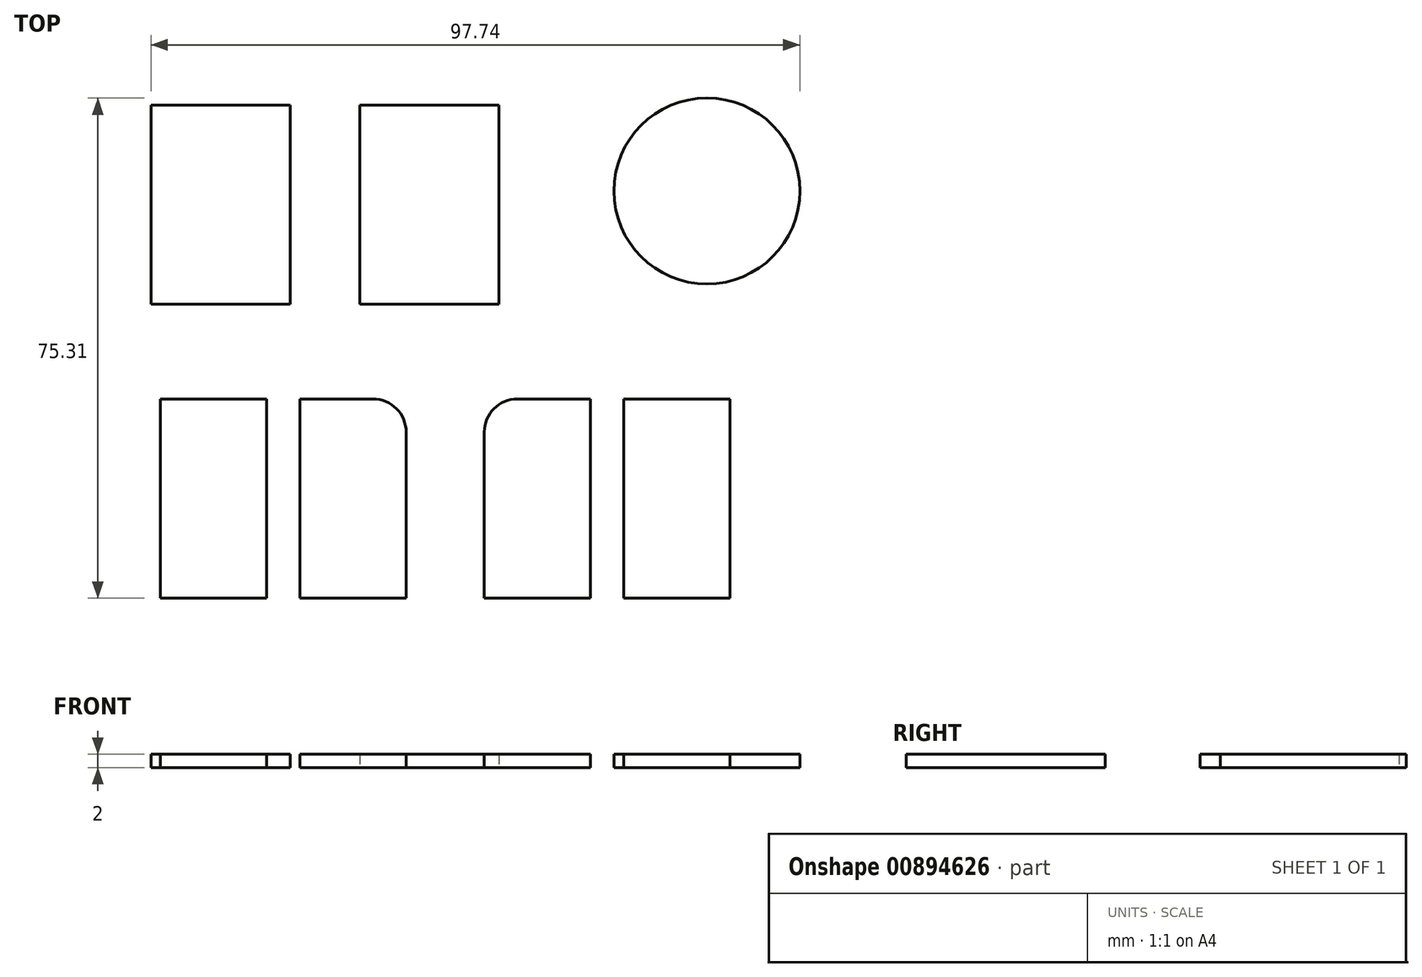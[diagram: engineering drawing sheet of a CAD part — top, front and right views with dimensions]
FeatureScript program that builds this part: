
annotation { "Feature Type Name" : "Feature", "Feature Type Description" : "" }
export const myFeature = defineFeature(function(context is Context, id is Id, definition is map)
    precondition{}
    {
        {
            var Q0;
            Q0=qCreatedBy(makeId("Top.planeOp"),FACE);
            var sketch = newSketch(context, id + "F0", { "sketchPlane" : qUnion([Q0])});
            skLineSegment(sketch, "E0.bottom", {"start": v(0, 0) * mm, "end": v(-21, 0) * mm});
            skLineSegment(sketch, "E0.top", {"start": v(0, 30) * mm, "end": v(-21, 30) * mm});
            skLineSegment(sketch, "E0.left", {"start": v(0, 0) * mm, "end": v(0, 30) * mm});
            skLineSegment(sketch, "E0.right", {"start": v(-21, 0) * mm, "end": v(-21, 30) * mm});
            skLineSegment(sketch, "E1.bottom", {"start": v(10.44, 0) * mm, "end": v(31.44, 0) * mm});
            skLineSegment(sketch, "E1.top", {"start": v(10.44, 30) * mm, "end": v(31.44, 30) * mm});
            skLineSegment(sketch, "E1.left", {"start": v(10.44, 0) * mm, "end": v(10.44, 30) * mm});
            skLineSegment(sketch, "E1.right", {"start": v(31.44, 0) * mm, "end": v(31.44, 30) * mm});
            skLineSegment(sketch, "E2.bottom", {"start": v(-19.56, -14.26) * mm, "end": v(-3.56, -14.26) * mm});
            skLineSegment(sketch, "E2.top", {"start": v(-19.56, -44.26) * mm, "end": v(-3.56, -44.26) * mm});
            skLineSegment(sketch, "E2.left", {"start": v(-19.56, -14.26) * mm, "end": v(-19.56, -44.26) * mm});
            skLineSegment(sketch, "E2.right", {"start": v(17.44, -19.26) * mm, "end": v(17.44, -44.26) * mm});
            skLineSegment(sketch, "E3.bottom", {"start": v(34.2, -14.26) * mm, "end": v(45.2, -14.26) * mm});
            skLineSegment(sketch, "E3.top", {"start": v(29.2, -44.26) * mm, "end": v(45.2, -44.26) * mm});
            skLineSegment(sketch, "E3.left", {"start": v(29.2, -19.26) * mm, "end": v(29.2, -44.26) * mm});
            skLineSegment(sketch, "E3.right", {"start": v(66.2, -14.26) * mm, "end": v(66.2, -44.26) * mm});
            skPoint(sketch, "E4.visualSharp", {"position": v(17.44, -14.26) * mm});
            skArc(sketch, "E4.filletArc", {"start": v(17.44, -19.26) * mm, "mid": v(15.98, -15.73) * mm, "end": v(12.44, -14.26) * mm});
            skPoint(sketch, "E5.visualSharp", {"position": v(29.2, -14.26) * mm});
            skArc(sketch, "E5.filletArc", {"start": v(34.2, -14.26) * mm, "mid": v(30.67, -15.73) * mm, "end": v(29.2, -19.26) * mm});
            skLineSegment(sketch, "E6", {"start": v(-3.56, -14.26) * mm, "end": v(-3.56, -44.26) * mm});
            skLineSegment(sketch, "E7", {"start": v(1.44, -14.26) * mm, "end": v(1.44, -44.26) * mm});
            skLineSegment(sketch, "E8", {"start": v(50.2, -14.26) * mm, "end": v(50.2, -44.26) * mm});
            skLineSegment(sketch, "E9", {"start": v(45.2, -14.26) * mm, "end": v(45.2, -44.26) * mm});
            skLineSegment(sketch, "E10.trimOffspring", {"start": v(1.44, -14.26) * mm, "end": v(12.44, -14.26) * mm});
            skLineSegment(sketch, "E11.trimOffspring", {"start": v(1.44, -44.26) * mm, "end": v(17.44, -44.26) * mm});
            skLineSegment(sketch, "E12.trimOffspring", {"start": v(50.2, -44.26) * mm, "end": v(66.2, -44.26) * mm});
            skLineSegment(sketch, "E13.trimOffspring", {"start": v(50.2, -14.26) * mm, "end": v(66.2, -14.26) * mm});
            skCircle(sketch, "E14", {"center": v(62.74, 17.05) * mm, "radius": 14 * mm});
            skSolve(sketch);
        }
        {
            var Q0;
            Q0 = qSketchRegion(id + "F0", true);
            extrude(context, id + "F1", {"entities" : qUnion([Q0]), "depth" : 2 * mm, "offsetDistance" : 25 * mm});
        }
    });
